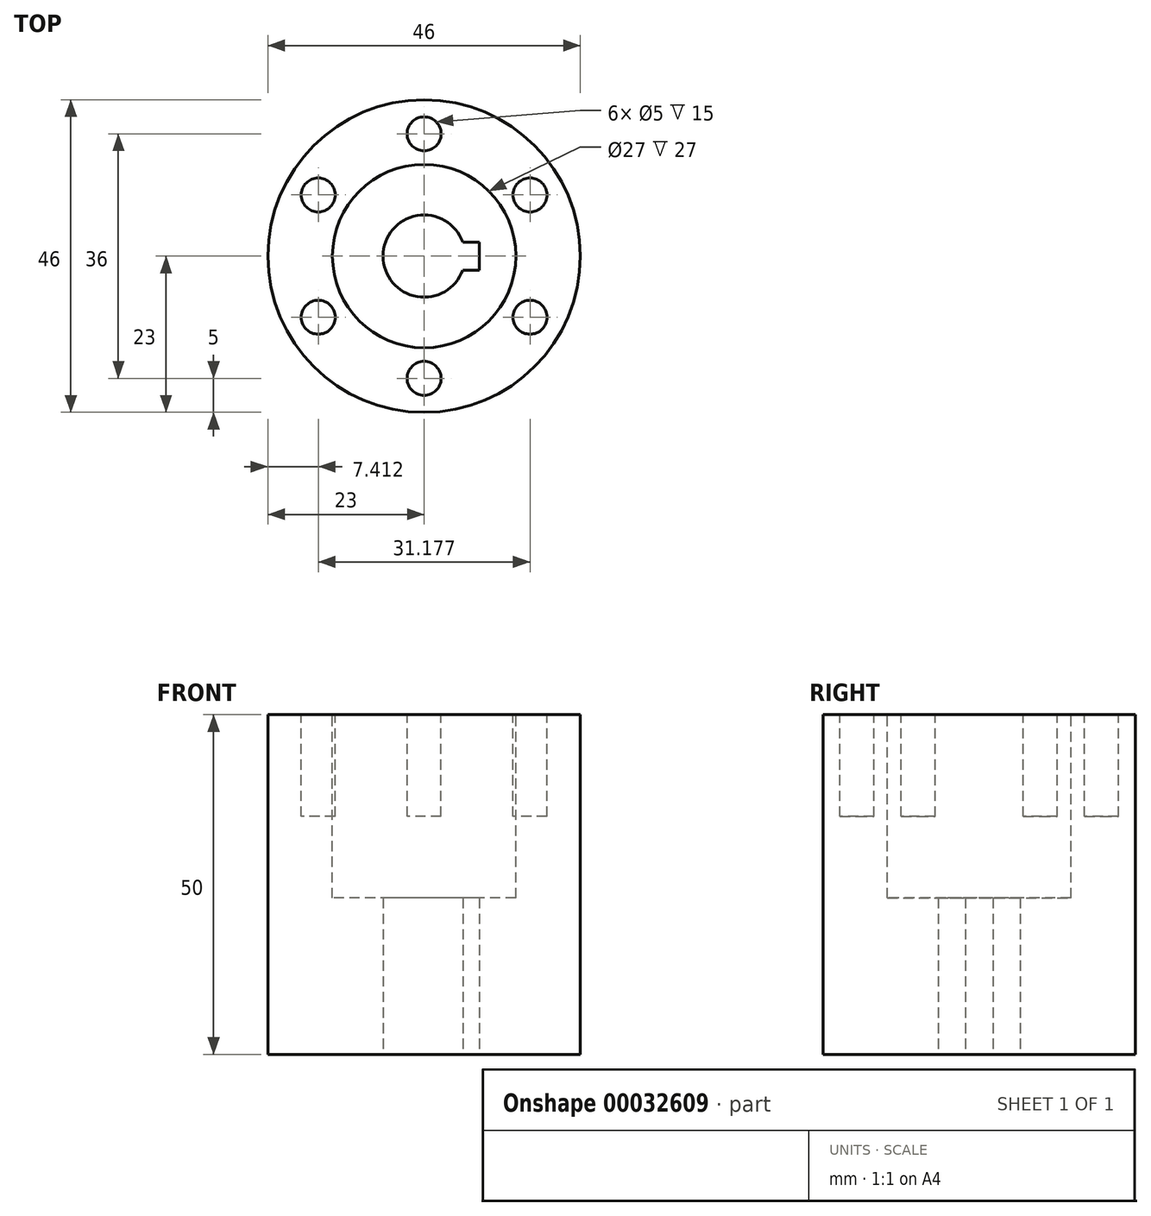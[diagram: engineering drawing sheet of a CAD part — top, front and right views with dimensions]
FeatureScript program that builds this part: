
annotation { "Feature Type Name" : "Feature", "Feature Type Description" : "" }
export const myFeature = defineFeature(function(context is Context, id is Id, definition is map)
    precondition{}
    {
        {
            var Q0;
            Q0=qCreatedBy(makeId("Top.planeOp"),FACE);
            var sketch = newSketch(context, id + "F0", { "sketchPlane" : qUnion([Q0])});
            skCircle(sketch, "E0", {"center": v(0, 0) * mm, "radius": 23 * mm});
            skCircle(sketch, "E1", {"center": v(0, 0) * mm, "radius": 6.05 * mm});
            skLineSegment(sketch, "E2.bottom", {"start": v(8.1, -2.05) * mm, "end": v(-8.1, -2.05) * mm});
            skLineSegment(sketch, "E2.top", {"start": v(8.1, 2.05) * mm, "end": v(-8.1, 2.05) * mm});
            skLineSegment(sketch, "E2.left", {"start": v(8.1, -2.05) * mm, "end": v(8.1, 2.05) * mm});
            skLineSegment(sketch, "E2.right", {"start": v(-8.1, -2.05) * mm, "end": v(-8.1, 2.05) * mm});
            skSolve(sketch);
        }
        {
            var Q0;
            Q0=makeQuery(id+"F0.imprint","IMPRINT",FACE,{"disambiguationData":[TD([[makeQuery(id+"F0.imprint","IMPRINT",EDGE,{"derivedFrom":sQuery(id+"F0.wireOp",EDGE,"E0")}),1.0]])]});
            var Q1;
            {var subQ5=sQuery(id+"F0.wireOp",EDGE,"E2.right");Q1=makeQuery(id+"F0.imprint","IMPRINT",FACE,{"disambiguationData":[TD([[makeQuery(id+"F0.imprint","IMPRINT",EDGE,{"derivedFrom":subQ5}),-1.0]])]});}
            extrude(context, id + "F3", {"entities" : qUnion([Q0, Q1]), "depth" : 50 * mm});
        }
        {
            var Q0;
            Q0=makeQuery(id+"F3.opExtrude","CAP_FACE",FACE,{"disambiguationData":[OSD([sQuery(id+"F0.wireOp",EDGE,"E0"),sQuery(id+"F0.wireOp",EDGE,"E1"),sQuery(id+"F0.wireOp",EDGE,"E2.bottom"),sQuery(id+"F0.wireOp",EDGE,"E2.top"),sQuery(id+"F0.wireOp",EDGE,"E2.left")])],"isStart":false});
            var sketch = newSketch(context, id + "F4", { "sketchPlane" : qUnion([Q0])});
            skCircle(sketch, "E3", {"center": v(0, 0) * mm, "radius": 13.5 * mm});
            skSolve(sketch);
        }
        {
            var Q0;
            Q0=makeQuery(id+"F4.imprint","IMPRINT",FACE,{"disambiguationData":[TD([[makeQuery(id+"F4.imprint","IMPRINT",EDGE,{"derivedFrom":sQuery(id+"F4.wireOp",EDGE,"E3")}),1.0]])]});
            extrude(context, id + "F1", {"entities" : qUnion([Q0]), "operationType" : NewBodyOperationType.REMOVE, "oppositeDirection" : true, "depth" : 27 * mm});
        }
        {
            var Q0;
            Q0=makeQuery(id+"F3.opExtrude","CAP_FACE",FACE,{"disambiguationData":[OSD([sQuery(id+"F0.wireOp",EDGE,"E0"),sQuery(id+"F0.wireOp",EDGE,"E1"),sQuery(id+"F0.wireOp",EDGE,"E2.bottom"),sQuery(id+"F0.wireOp",EDGE,"E2.top"),sQuery(id+"F0.wireOp",EDGE,"E2.left")])],"isStart":false});
            var sketch = newSketch(context, id + "F5", { "sketchPlane" : qUnion([Q0])});
            skCircle(sketch, "E4.cCircle", {"center": v(0, 0) * mm, "radius": 15.59 * mm, "construction": true});
            skLineSegment(sketch, "E4.0", {"start": v(15.59, 9) * mm, "end": v(15.59, -9) * mm, "construction": true});
            skLineSegment(sketch, "E4.1", {"start": v(15.59, -9) * mm, "end": v(0, -18) * mm, "construction": true});
            skLineSegment(sketch, "E4.2", {"start": v(0, -18) * mm, "end": v(-15.59, -9) * mm, "construction": true});
            skLineSegment(sketch, "E4.3", {"start": v(-15.59, -9) * mm, "end": v(-15.59, 9) * mm, "construction": true});
            skLineSegment(sketch, "E4.4", {"start": v(-15.59, 9) * mm, "end": v(0, 18) * mm, "construction": true});
            skLineSegment(sketch, "E4.5", {"start": v(0, 18) * mm, "end": v(15.59, 9) * mm, "construction": true});
            skPoint(sketch, "E4.0.midPoint", {"position": v(15.59, 0) * mm});
            skCircle(sketch, "E5", {"center": v(15.59, 9) * mm, "radius": 2.5 * mm});
            skCircle(sketch, "E6", {"center": v(15.59, -9) * mm, "radius": 2.5 * mm});
            skCircle(sketch, "E7", {"center": v(0, -18) * mm, "radius": 2.5 * mm});
            skCircle(sketch, "E8", {"center": v(-15.59, -9) * mm, "radius": 2.5 * mm});
            skCircle(sketch, "E9", {"center": v(-15.59, 9) * mm, "radius": 2.5 * mm});
            skCircle(sketch, "E10", {"center": v(0, 18) * mm, "radius": 2.5 * mm});
            skSolve(sketch);
        }
        {
            var Q0;
            Q0=makeQuery(id+"F5.imprint","IMPRINT",FACE,{"disambiguationData":[TD([[makeQuery(id+"F5.imprint","IMPRINT",EDGE,{"derivedFrom":sQuery(id+"F5.wireOp",EDGE,"E5")}),1.0]])]});
            var Q1;
            Q1=makeQuery(id+"F5.imprint","IMPRINT",FACE,{"disambiguationData":[TD([[makeQuery(id+"F5.imprint","IMPRINT",EDGE,{"derivedFrom":sQuery(id+"F5.wireOp",EDGE,"E10")}),1.0]])]});
            var Q2;
            Q2=makeQuery(id+"F5.imprint","IMPRINT",FACE,{"disambiguationData":[TD([[makeQuery(id+"F5.imprint","IMPRINT",EDGE,{"derivedFrom":sQuery(id+"F5.wireOp",EDGE,"E9")}),1.0]])]});
            var Q3;
            Q3=makeQuery(id+"F5.imprint","IMPRINT",FACE,{"disambiguationData":[TD([[makeQuery(id+"F5.imprint","IMPRINT",EDGE,{"derivedFrom":sQuery(id+"F5.wireOp",EDGE,"E6")}),1.0]])]});
            var Q4;
            Q4=makeQuery(id+"F5.imprint","IMPRINT",FACE,{"disambiguationData":[TD([[makeQuery(id+"F5.imprint","IMPRINT",EDGE,{"derivedFrom":sQuery(id+"F5.wireOp",EDGE,"E7")}),1.0]])]});
            var Q5;
            Q5=makeQuery(id+"F5.imprint","IMPRINT",FACE,{"disambiguationData":[TD([[makeQuery(id+"F5.imprint","IMPRINT",EDGE,{"derivedFrom":sQuery(id+"F5.wireOp",EDGE,"E8")}),1.0]])]});
            extrude(context, id + "F2", {"entities" : qUnion([Q0, Q1, Q2, Q3, Q4, Q5]), "operationType" : NewBodyOperationType.REMOVE, "oppositeDirection" : true, "depth" : 15 * mm});
        }
    });
